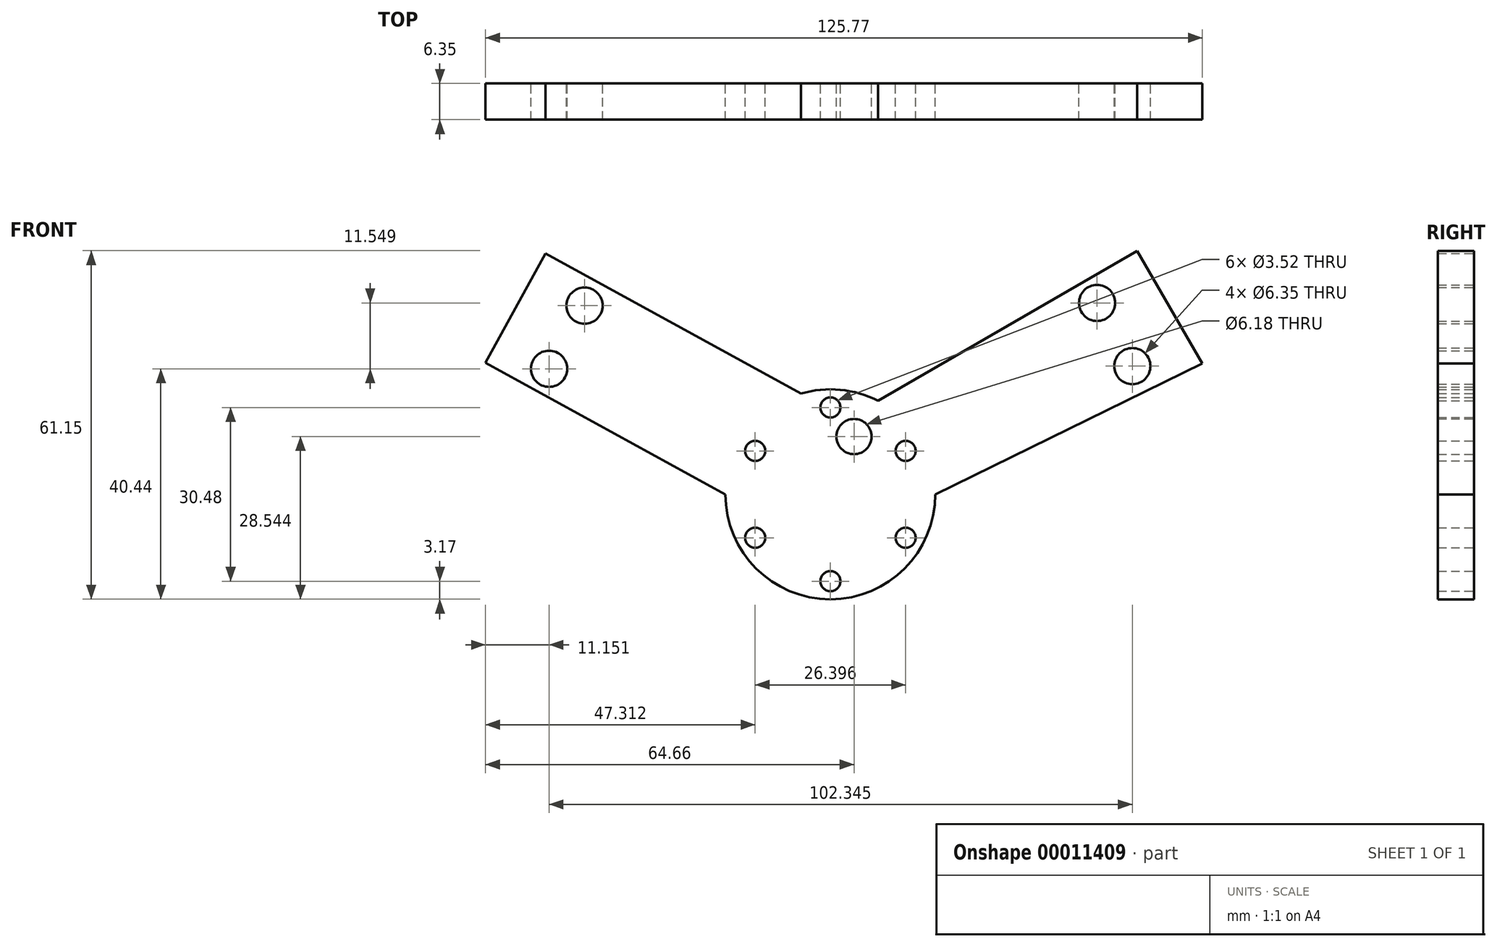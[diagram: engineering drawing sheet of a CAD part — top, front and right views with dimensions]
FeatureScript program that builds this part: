
annotation { "Feature Type Name" : "Feature", "Feature Type Description" : "" }
export const myFeature = defineFeature(function(context is Context, id is Id, definition is map)
    precondition{}
    {
        {
            var Q0;
            Q0=qCreatedBy(makeId("Front.planeOp"),FACE);
            var sketch = newSketch(context, id + "F0", { "sketchPlane" : qUnion([Q0])});
            skCircle(sketch, "E0", {"center": v(0, 0) * mm, "radius": 18.41 * mm});
            skCircle(sketch, "E1", {"center": v(0, 0) * mm, "radius": 15.24 * mm, "construction": true});
            skCircle(sketch, "E2", {"center": v(0, 15.24) * mm, "radius": 1.76 * mm});
            skCircle(sketch, "E3.1.0", {"center": v(-13.2, 7.62) * mm, "radius": 1.76 * mm});
            skCircle(sketch, "E3.2.0", {"center": v(-13.2, -7.62) * mm, "radius": 1.76 * mm});
            skCircle(sketch, "E3.3.0", {"center": v(0, -15.24) * mm, "radius": 1.76 * mm});
            skCircle(sketch, "E3.4.0", {"center": v(13.2, -7.62) * mm, "radius": 1.76 * mm});
            skCircle(sketch, "E3.5.0", {"center": v(13.2, 7.62) * mm, "radius": 1.76 * mm});
            skLineSegment(sketch, "E4", {"start": v(8.37, 16.4) * mm, "end": v(53.8, 42.74) * mm});
            skLineSegment(sketch, "E5", {"start": v(53.8, 42.74) * mm, "end": v(65.26, 22.97) * mm});
            skLineSegment(sketch, "E6", {"start": v(65.26, 22.97) * mm, "end": v(18.42, 0) * mm});
            skLineSegment(sketch, "E7", {"start": v(-18.41, 0) * mm, "end": v(-60.51, 23.07) * mm});
            skLineSegment(sketch, "E8", {"start": v(-60.51, 23.07) * mm, "end": v(-50, 42.25) * mm});
            skLineSegment(sketch, "E9", {"start": v(-50, 42.25) * mm, "end": v(-5.16, 17.68) * mm});
            skCircle(sketch, "E10", {"center": v(4.15, 10.13) * mm, "radius": 3.09 * mm});
            skCircle(sketch, "E11", {"center": v(-43.14, 33.1) * mm, "radius": 3.18 * mm});
            skCircle(sketch, "E12", {"center": v(-49.36, 22.03) * mm, "radius": 3.18 * mm});
            skCircle(sketch, "E13", {"center": v(46.8, 33.58) * mm, "radius": 3.18 * mm});
            skCircle(sketch, "E14", {"center": v(52.99, 22.49) * mm, "radius": 3.18 * mm});
            skSolve(sketch);
        }
        {
            var Q0;
            Q0 = qSketchRegion(id + "F0", true);
            extrude(context, id + "F1", {"entities" : qUnion([Q0]), "depth" : 6.35 * mm});
        }
    });
